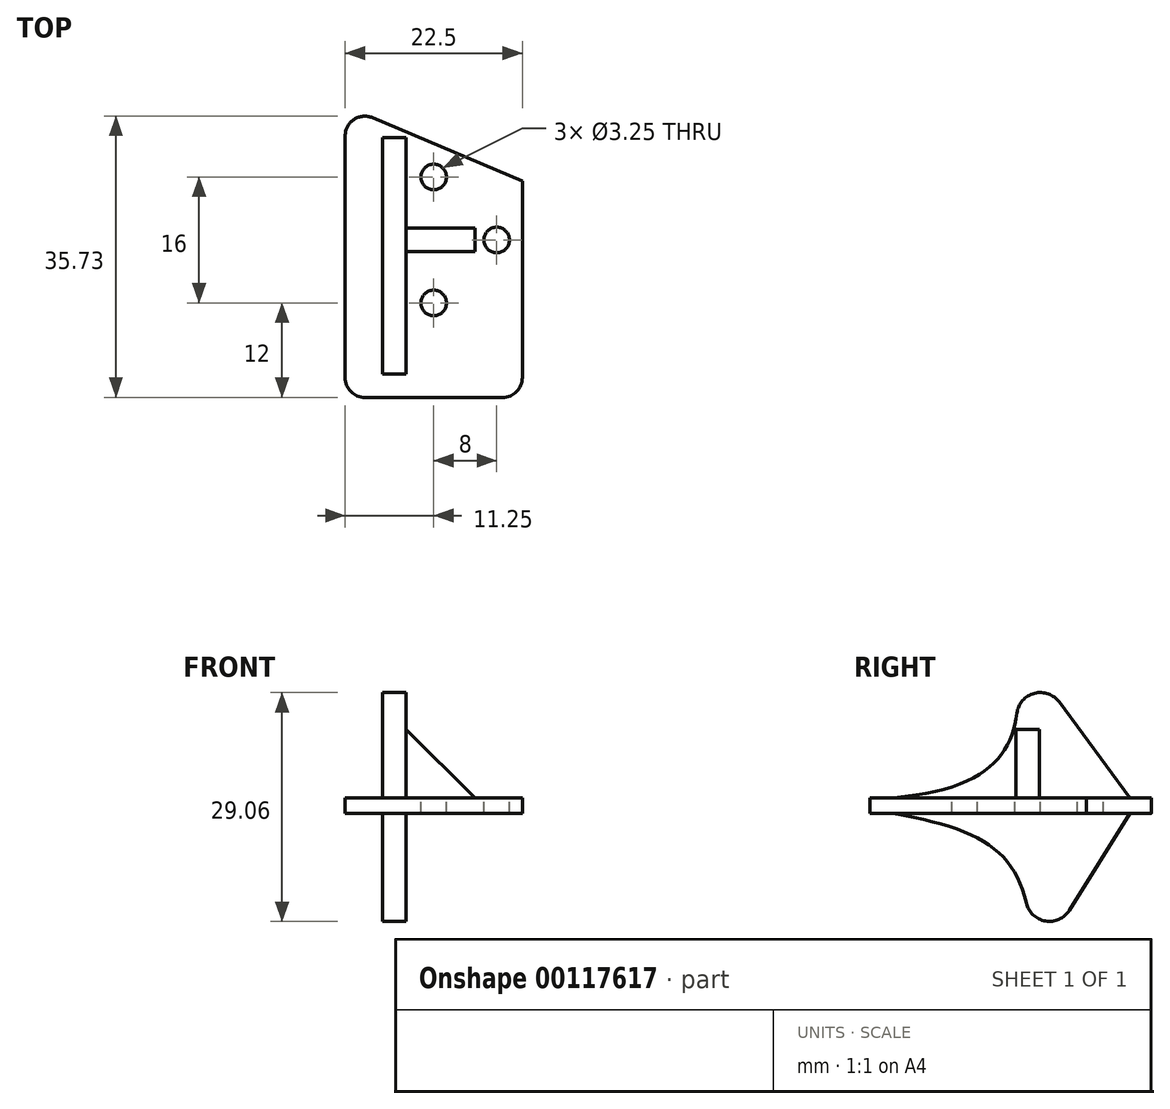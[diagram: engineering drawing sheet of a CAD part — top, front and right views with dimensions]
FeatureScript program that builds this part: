
annotation { "Feature Type Name" : "Feature", "Feature Type Description" : "" }
export const myFeature = defineFeature(function(context is Context, id is Id, definition is map)
    precondition{}
    {
        {
            var Q0;
            Q0=qCreatedBy(makeId("Top.planeOp"),FACE);
            var sketch = newSketch(context, id + "F0", { "sketchPlane" : qUnion([Q0])});
            skLineSegment(sketch, "E0.bottom", {"start": v(-11.25, 18.5) * mm, "end": v(11.25, 18.5) * mm});
            skLineSegment(sketch, "E0.top", {"start": v(-11.25, -18.5) * mm, "end": v(11.25, -18.5) * mm});
            skLineSegment(sketch, "E0.left", {"start": v(-11.25, 18.5) * mm, "end": v(-11.25, -18.5) * mm});
            skLineSegment(sketch, "E0.right", {"start": v(11.25, 18.5) * mm, "end": v(11.25, -18.5) * mm});
            skPoint(sketch, "E0.middle", {"position": v(0, 0) * mm});
            skSolve(sketch);
        }
        {
            var Q0;
            Q0=makeQuery(id+"F0.imprint","IMPRINT",FACE,{"disambiguationData":[TD([[makeQuery(id+"F0.imprint","IMPRINT",EDGE,{"derivedFrom":sQuery(id+"F0.wireOp",EDGE,"E0.bottom")}),-1.0]])]});
            extrude(context, id + "F1", {"entities" : qUnion([Q0]), "depth" : 2 * mm});
        }
        {
            var Q0;
            Q0=makeQuery(id+"F1.opExtrude","CAP_FACE",FACE,{"disambiguationData":[OSD([sQuery(id+"F0.wireOp",EDGE,"E0.bottom"),sQuery(id+"F0.wireOp",EDGE,"E0.top"),sQuery(id+"F0.wireOp",EDGE,"E0.left"),sQuery(id+"F0.wireOp",EDGE,"E0.right")])],"isStart":false});
            var sketch = newSketch(context, id + "F2", { "sketchPlane" : qUnion([Q0])});
            skCircle(sketch, "E1", {"center": v(0, -6.5) * mm, "radius": 1.75 * mm});
            skCircle(sketch, "E2", {"center": v(0, 9.5) * mm, "radius": 1.75 * mm});
            skLineSegment(sketch, "E3", {"start": v(0, 9.5) * mm, "end": v(0, -6.5) * mm, "construction": true});
            skLineSegment(sketch, "E4", {"start": v(0, 1.5) * mm, "end": v(8, 1.5) * mm, "construction": true});
            skCircle(sketch, "E5", {"center": v(8, 1.5) * mm, "radius": 1.7 * mm});
            skSolve(sketch);
        }
        {
            var Q0;
            Q0=makeQuery(id+"F2.imprint","IMPRINT",FACE,{"disambiguationData":[TD([[makeQuery(id+"F2.imprint","IMPRINT",EDGE,{"derivedFrom":sQuery(id+"F2.wireOp",EDGE,"E1")}),-1.0]])]});
            var sketch = newSketch(context, id + "F3", { "sketchPlane" : qUnion([Q0])});
            skLineSegment(sketch, "E6", {"start": v(-11.25, 18.5) * mm, "end": v(11.25, 9) * mm});
            skLineSegment(sketch, "E7", {"start": v(-11.25, 18.5) * mm, "end": v(11.25, 18.5) * mm});
            skLineSegment(sketch, "E8", {"start": v(11.25, 18.5) * mm, "end": v(11.25, 9) * mm});
            skSolve(sketch);
        }
        {
            var Q0;
            Q0=makeQuery(id+"F3.imprint","IMPRINT",FACE,{"disambiguationData":[TD([[makeQuery(id+"F3.imprint","IMPRINT",EDGE,{"derivedFrom":sQuery(id+"F3.wireOp",EDGE,"E6")}),1.0]])]});
            extrude(context, id + "F4", {"entities" : qUnion([Q0]), "operationType" : NewBodyOperationType.REMOVE, "endBound" : BoundingType.THROUGH_ALL, "oppositeDirection" : true, "depth" : 25 * mm});
        }
        {
            var Q0;
            Q0=makeQuery(id+"F4.boolean.opBoolean","COPY",EDGE,{"derivedFrom":makeQuery(id+"F4.opExtrude","SWEPT_EDGE",EDGE,{"disambiguationData":[OSD([sQuery(id+"F0.wireOp",EDGE,"E0.right"),sQuery(id+"F3.wireOp",EDGE,"E6"),sQuery(id+"F3.wireOp",EDGE,"E8")])]})});
            var Q1;
            Q1=makeQuery(id+"F1.opExtrude","SWEPT_EDGE",EDGE,{"disambiguationData":[OSD([sQuery(id+"F0.wireOp",EDGE,"E0.top"),sQuery(id+"F0.wireOp",EDGE,"E0.right")])]});
            var Q2;
            Q2=makeQuery(id+"F1.opExtrude","SWEPT_EDGE",EDGE,{"disambiguationData":[OSD([sQuery(id+"F0.wireOp",EDGE,"E0.top"),sQuery(id+"F0.wireOp",EDGE,"E0.left")])]});
            var Q3;
            {var subQ0=sQuery(id+"F0.wireOp",EDGE,"E0.left");Q3=makeQuery(id+"F4.boolean.opBoolean","MERGE",EDGE,{"derivedFrom":[makeQuery(id+"F1.opExtrude","SWEPT_EDGE",EDGE,{"disambiguationData":[OSD([sQuery(id+"F0.wireOp",EDGE,"E0.bottom"),subQ0])]}),makeQuery(id+"F4.opExtrude","SWEPT_EDGE",EDGE,{"disambiguationData":[OSD([subQ0,sQuery(id+"F3.wireOp",EDGE,"E6"),sQuery(id+"F3.wireOp",EDGE,"E7")])]})]});}
            fillet(context, id + "F5", {"entities" : qUnion([Q0, Q1, Q2, Q3]), "radius" : 2.5 * mm, "tangentPropagation" : true, "allowEdgeOverflow" : false});
        }
        {
            var Q0;
            Q0=sQuery(id+"F2.wireOp",VERTEX,"E2.center");
            var Q1;
            Q1=sQuery(id+"F2.wireOp",VERTEX,"E1.center");
            var Q2;
            Q2=sQuery(id+"F2.wireOp",VERTEX,"E5.center");
            var Q3;
            Q3=makeQuery(id+"F1.opExtrude","SWEPT_BODY",BODY,{"disambiguationData":[OSD([sQuery(id+"F0.wireOp",EDGE,"E0.bottom"),sQuery(id+"F0.wireOp",EDGE,"E0.top"),sQuery(id+"F0.wireOp",EDGE,"E0.left"),sQuery(id+"F0.wireOp",EDGE,"E0.right")])]});
            hole(context, id + "F6", {"style" : HoleStyle.SIMPLE, "endStyle" : HoleEndStyle.BLIND, "holeDiameter" : 3.25 * mm, "holeDepth" : 8 * mm, "locations" : qUnion([Q0, Q1, Q2]), "scope" : qUnion([Q3])});
        }
        {
            var Q0;
            Q0=qCreatedBy(makeId("Right.planeOp"),FACE);
            cPlane(context, id + "F7", {"entities" : qUnion([Q0]), "cplaneType" : CPlaneType.OFFSET, "offset" : 5 * mm, "oppositeDirection" : true, "width" : 150 * mm, "height" : 150 * mm});
        }
        {
            var Q0;
            Q0=qCreatedBy(id+"F7.planeOp",FACE);
            var sketch = newSketch(context, id + "F8", { "sketchPlane" : qUnion([Q0])});
            skLineSegment(sketch, "E9", {"start": v(14.5, 2) * mm, "end": v(0, 21.67) * mm});
            skFitSpline(sketch, "E10", {"points": [v(0, 21.67) * mm, v(-15.5, 2) * mm], "startDerivative": vector(2.42, -29.6) * mm, "endDerivative": vector(-51.1, -4.52) * mm});
            skLineSegment(sketch, "E11", {"start": v(14.5, 2) * mm, "end": v(-15.5, 2) * mm});
            skSolve(sketch);
        }
        {
            var Q0;
            Q0=makeQuery(id+"F8.imprint","IMPRINT",FACE,{"disambiguationData":[TD([[makeQuery(id+"F8.imprint","IMPRINT",EDGE,{"derivedFrom":sQuery(id+"F8.wireOp",EDGE,"E9")}),1.0]])]});
            extrude(context, id + "F9", {"entities" : qUnion([Q0]), "operationType" : NewBodyOperationType.ADD, "endBound" : BoundingType.SYMMETRIC, "depth" : 3 * mm});
        }
        {
            var Q0;
            Q0=makeQuery(id+"F9.opExtrude","SWEPT_EDGE",EDGE,{"disambiguationData":[OSD([sQuery(id+"F8.wireOp",EDGE,"E9"),sQuery(id+"F8.wireOp",EDGE,"E10")])]});
            fillet(context, id + "F10", {"entities" : qUnion([Q0]), "radius" : 3 * mm, "tangentPropagation" : true, "allowEdgeOverflow" : false});
        }
        {
            var Q0;
            Q0=makeQuery(id+"F1.opExtrude","SWEPT_BODY",BODY,{"disambiguationData":[OSD([sQuery(id+"F0.wireOp",EDGE,"E0.bottom"),sQuery(id+"F0.wireOp",EDGE,"E0.top"),sQuery(id+"F0.wireOp",EDGE,"E0.left"),sQuery(id+"F0.wireOp",EDGE,"E0.right")])]});
            transform(context, id + "F11", {"entities" : qUnion([Q0]), "transformType" : TransformType.TRANSLATION_3D, "dx" : 0 * mm, "dy" : 0 * mm, "dz" : 0 * mm, "makeCopy" : true});
        }
        {
            var Q0;
            Q0=qCreatedBy(id+"F7.planeOp",FACE);
            var sketch = newSketch(context, id + "F12", { "sketchPlane" : qUnion([Q0])});
            skLineSegment(sketch, "E12", {"start": v(14.5, 0) * mm, "end": v(2, -20) * mm});
            skLineSegment(sketch, "E13", {"start": v(-15.5, 0) * mm, "end": v(14.5, 0) * mm});
            skFitSpline(sketch, "E14", {"points": [v(-15.5, 0) * mm, v(2, -20) * mm], "startDerivative": vector(41.85, -7.35) * mm, "endDerivative": vector(-0.9, -41.45) * mm});
            skSolve(sketch);
        }
        {
            var Q0;
            Q0=makeQuery(id+"F12.imprint","IMPRINT",FACE,{"disambiguationData":[TD([[makeQuery(id+"F12.imprint","IMPRINT",EDGE,{"derivedFrom":sQuery(id+"F12.wireOp",EDGE,"E12")}),-1.0]])]});
            extrude(context, id + "F13", {"entities" : qUnion([Q0]), "operationType" : NewBodyOperationType.ADD, "endBound" : BoundingType.SYMMETRIC, "depth" : 3 * mm});
        }
        {
            var Q0;
            Q0=makeQuery(id+"F13.opExtrude","SWEPT_EDGE",EDGE,{"disambiguationData":[OSD([sQuery(id+"F12.wireOp",EDGE,"E12"),sQuery(id+"F12.wireOp",EDGE,"E14")])]});
            fillet(context, id + "F14", {"entities" : qUnion([Q0]), "radius" : 3 * mm, "tangentPropagation" : true, "allowEdgeOverflow" : false});
        }
        {
            var Q0;
            Q0=qCreatedBy(makeId("Front.planeOp"),FACE);
            var sketch = newSketch(context, id + "F15", { "sketchPlane" : qUnion([Q0])});
            skLineSegment(sketch, "E15", {"start": v(-3.78, 2) * mm, "end": v(-3.78, 10.99) * mm});
            skLineSegment(sketch, "E16", {"start": v(-3.78, 10.99) * mm, "end": v(5.25, 2) * mm});
            skLineSegment(sketch, "E17", {"start": v(5.25, 2) * mm, "end": v(-3.78, 2) * mm});
            skSolve(sketch);
        }
        {
            var Q0;
            Q0=makeQuery(id+"F15.imprint","IMPRINT",FACE,{"disambiguationData":[TD([[makeQuery(id+"F15.imprint","IMPRINT",EDGE,{"derivedFrom":sQuery(id+"F15.wireOp",EDGE,"E15")}),-1.0]])]});
            extrude(context, id + "F16", {"entities" : qUnion([Q0]), "operationType" : NewBodyOperationType.ADD, "oppositeDirection" : true, "depth" : 3 * mm});
        }
    });
